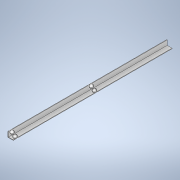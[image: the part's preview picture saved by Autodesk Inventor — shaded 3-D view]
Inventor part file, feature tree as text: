
AUTODESK INVENTOR PART (.ipt)
format: ipt  version: 2020.2 (Build 242310000, 310)  size: 143,872 bytes
history: native  units: in
note: dims shown in document units (in); Inventor stores cm internally (conversion verified against a paired STEP export)
features: sketch x3, hole x2, extrude x1
ambient origin geometry x8: Origin, YZ Plane, XZ Plane, XY Plane, X Axis, Y Axis, Z Axis, Center Point
bodies: Solid1 (feature_tree)
feature tree (6):
  extrude  "Extrusion1"  Depth=0.1181in
  hole  "Hole1"  [1 undecoded]
  hole  "Hole2"  [1 undecoded]
  sketch  "Sketch1"  dims[d0=0.1181in d1=0.1181in]
  sketch  "Sketch2"  dims[d2=1.1811in d3=1.1811in]
  sketch  "Sketch3"  dims[d4=35.4331in d5=0.0in d6=0.5906in d7=0.5906in d8=1.063in d9=0.5906in d10=17.7165in d11=17.7165in d12=0.5906in d13=17.7165in d14=0.5906in d15=0.15in d16=0.2953in d17=0.1476in d18=0.0984in d19=90.0deg d20=0.3937in d21=0.8108in d22=0.5906in d23=0.5906in d24=0.5906in d25=17.7165in d26=17.7165in d27=0.5906in d28=17.7165in d29=0.5906in d30=0.15in d31=0.2953in d32=0.1476in d33=0.0984in d34=90.0deg d35=0.3937in d36=0.8108in d41=0.0in d42=0.0in d43=0.0in d44=0.0in]
note: 2 required parameter values undecoded (feature->parameter linkage not recoverable at this tier; creation-order binding heuristic only, values carry confidence <= 0.55)
